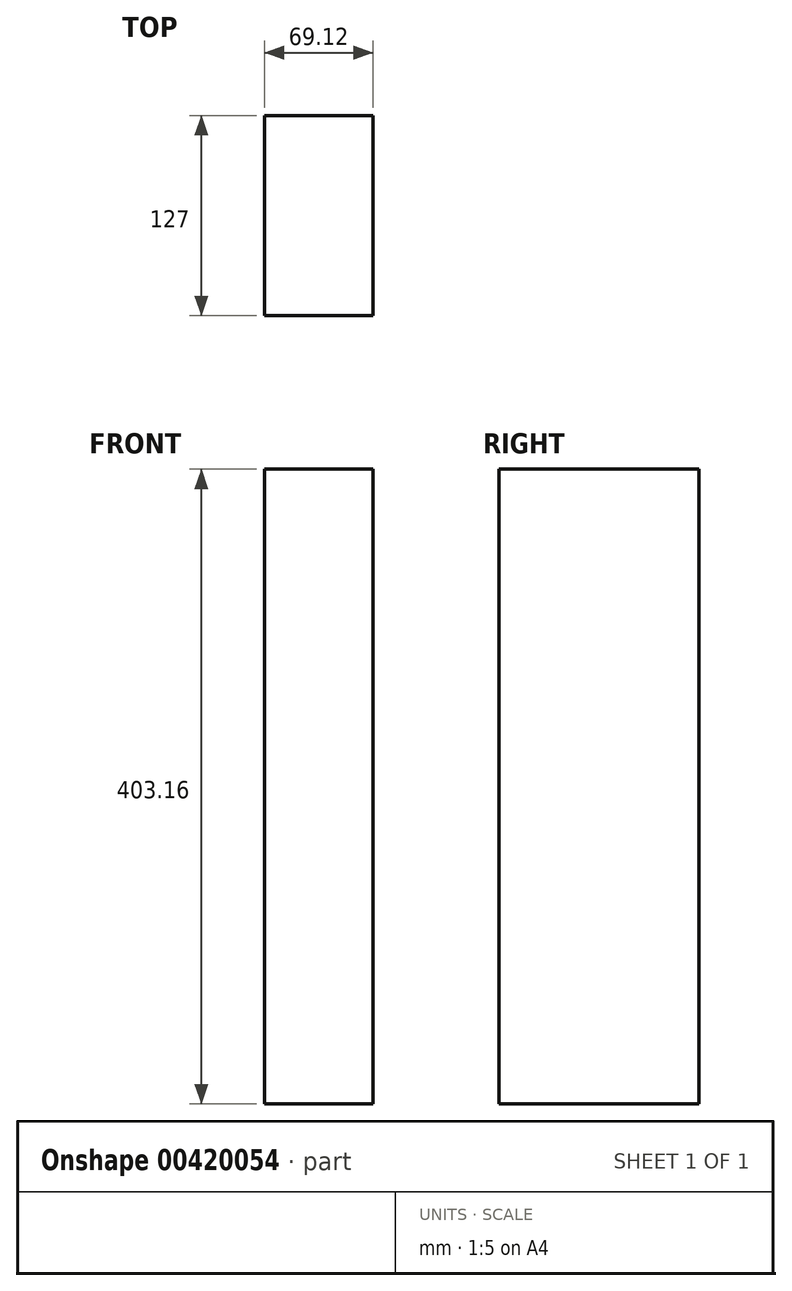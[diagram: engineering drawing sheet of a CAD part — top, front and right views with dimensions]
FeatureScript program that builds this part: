
annotation { "Feature Type Name" : "Feature", "Feature Type Description" : "" }
export const myFeature = defineFeature(function(context is Context, id is Id, definition is map)
    precondition{}
    {
        {
            var Q0;
            Q0=qCreatedBy(makeId("Front.planeOp"),FACE);
            var sketch = newSketch(context, id + "F0", { "sketchPlane" : qUnion([Q0])});
            skLineSegment(sketch, "E0.bottom", {"start": v(34.56, 201.58) * mm, "end": v(-34.56, 201.58) * mm});
            skLineSegment(sketch, "E0.top", {"start": v(34.56, -201.58) * mm, "end": v(-34.56, -201.58) * mm});
            skLineSegment(sketch, "E0.left", {"start": v(34.56, 201.58) * mm, "end": v(34.56, -201.58) * mm});
            skLineSegment(sketch, "E0.right", {"start": v(-34.56, 201.58) * mm, "end": v(-34.56, -201.58) * mm});
            skPoint(sketch, "E0.middle", {"position": v(0, 0) * mm});
            skSolve(sketch);
        }
        {
            var Q0;
            Q0=makeQuery(id+"F0.imprint","IMPRINT",FACE,{"disambiguationData":[TD([[makeQuery(id+"F0.imprint","IMPRINT",EDGE,{"derivedFrom":sQuery(id+"F0.wireOp",EDGE,"E0.bottom")}),1.0]])]});
            extrude(context, id + "F1", {"entities" : qUnion([Q0]), "depth" : 127 * mm});
        }
    });
